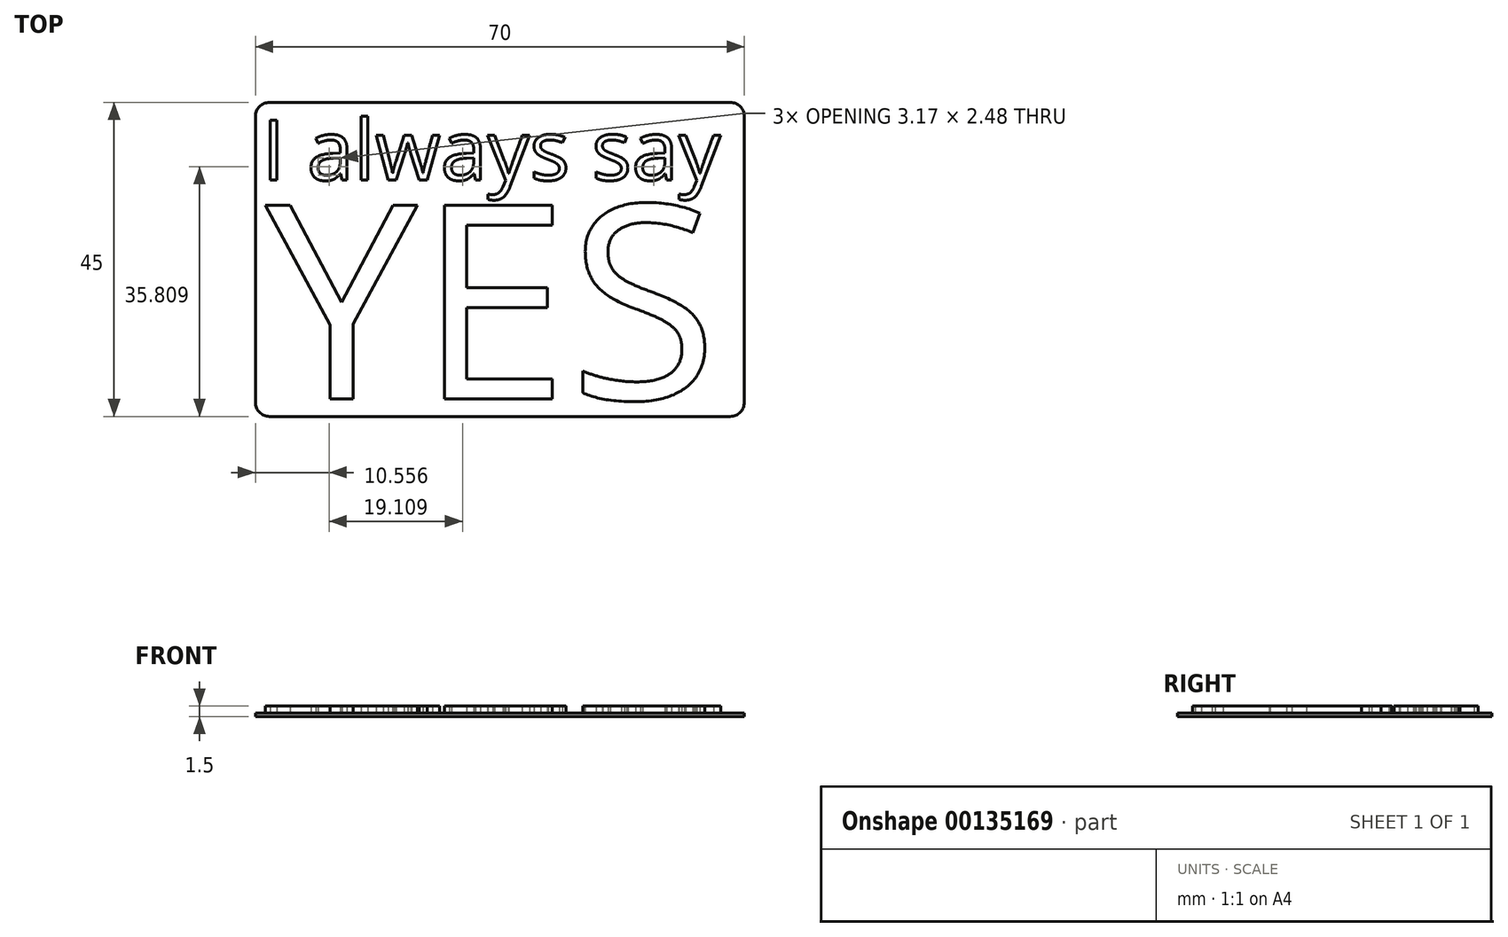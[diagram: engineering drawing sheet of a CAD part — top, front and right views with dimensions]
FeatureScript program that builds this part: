
annotation { "Feature Type Name" : "Feature", "Feature Type Description" : "" }
export const myFeature = defineFeature(function(context is Context, id is Id, definition is map)
    precondition{}
    {
        {
            var Q0;
            Q0=qCreatedBy(makeId("Top.planeOp"),FACE);
            var sketch = newSketch(context, id + "F0", { "sketchPlane" : qUnion([Q0])});
            skLineSegment(sketch, "E0.bottom", {"start": v(-12.44, 6.46) * mm, "end": v(57.56, 6.46) * mm});
            skLineSegment(sketch, "E0.top", {"start": v(-12.44, -38.54) * mm, "end": v(57.56, -38.54) * mm});
            skLineSegment(sketch, "E0.left", {"start": v(-12.44, 6.46) * mm, "end": v(-12.44, -38.54) * mm});
            skLineSegment(sketch, "E0.right", {"start": v(57.56, 6.46) * mm, "end": v(57.56, -38.54) * mm});
            skPoint(sketch, "E1", {"position": v(22.56, 6.46) * mm});
            skSolve(sketch);
        }
        {
            var Q0;
            Q0=qCreatedBy(makeId("Top.planeOp"),FACE);
            var sketch = newSketch(context, id + "F1", { "sketchPlane" : qUnion([Q0])});
            skText(sketch, "E2", { "text": "YES", "fontName": "OpenSans-Regular.ttf"});
            skText(sketch, "E3", { "text": "I always say", "fontName": "OpenSans-Regular.ttf"});
            const initialGuessF1  = {"E2": [-0.01099, -0.03603, 1, 0, 0.028], "E3": [-0.01153, -0.00466, 1, 0, 0.00867]};
            skSetInitialGuess(sketch, initialGuessF1);
            skSolve(sketch);
        }
        {
            var Q0;
            Q0 = qSketchRegion(id + "F1", true);
            extrude(context, id + "F2", {"entities" : qUnion([Q0]), "depth" : 1 * mm});
        }
        {
            var Q0;
            Q0 = qSketchRegion(id + "F0", true);
            extrude(context, id + "F3", {"entities" : qUnion([Q0]), "oppositeDirection" : true, "depth" : 0.5 * mm});
        }
        {
            var Q0;
            Q0=makeQuery(id+"F3.opExtrude","SWEPT_EDGE",EDGE,{"disambiguationData":[OSD([sQuery(id+"F0.wireOp",EDGE,"E0.top"),sQuery(id+"F0.wireOp",EDGE,"E0.right")])]});
            var Q1;
            Q1=makeQuery(id+"F3.opExtrude","SWEPT_EDGE",EDGE,{"disambiguationData":[OSD([sQuery(id+"F0.wireOp",EDGE,"E0.top"),sQuery(id+"F0.wireOp",EDGE,"E0.left")])]});
            var Q2;
            Q2=makeQuery(id+"F3.opExtrude","SWEPT_EDGE",EDGE,{"disambiguationData":[OSD([sQuery(id+"F0.wireOp",EDGE,"E0.bottom"),sQuery(id+"F0.wireOp",EDGE,"E0.right")])]});
            var Q3;
            Q3=makeQuery(id+"F3.opExtrude","SWEPT_EDGE",EDGE,{"disambiguationData":[OSD([sQuery(id+"F0.wireOp",EDGE,"E0.bottom"),sQuery(id+"F0.wireOp",EDGE,"E0.left")])]});
            fillet(context, id + "F4", {"entities" : qUnion([Q0, Q1, Q2, Q3]), "radius" : 2 * mm, "tangentPropagation" : true, "allowEdgeOverflow" : false});
        }
    });
